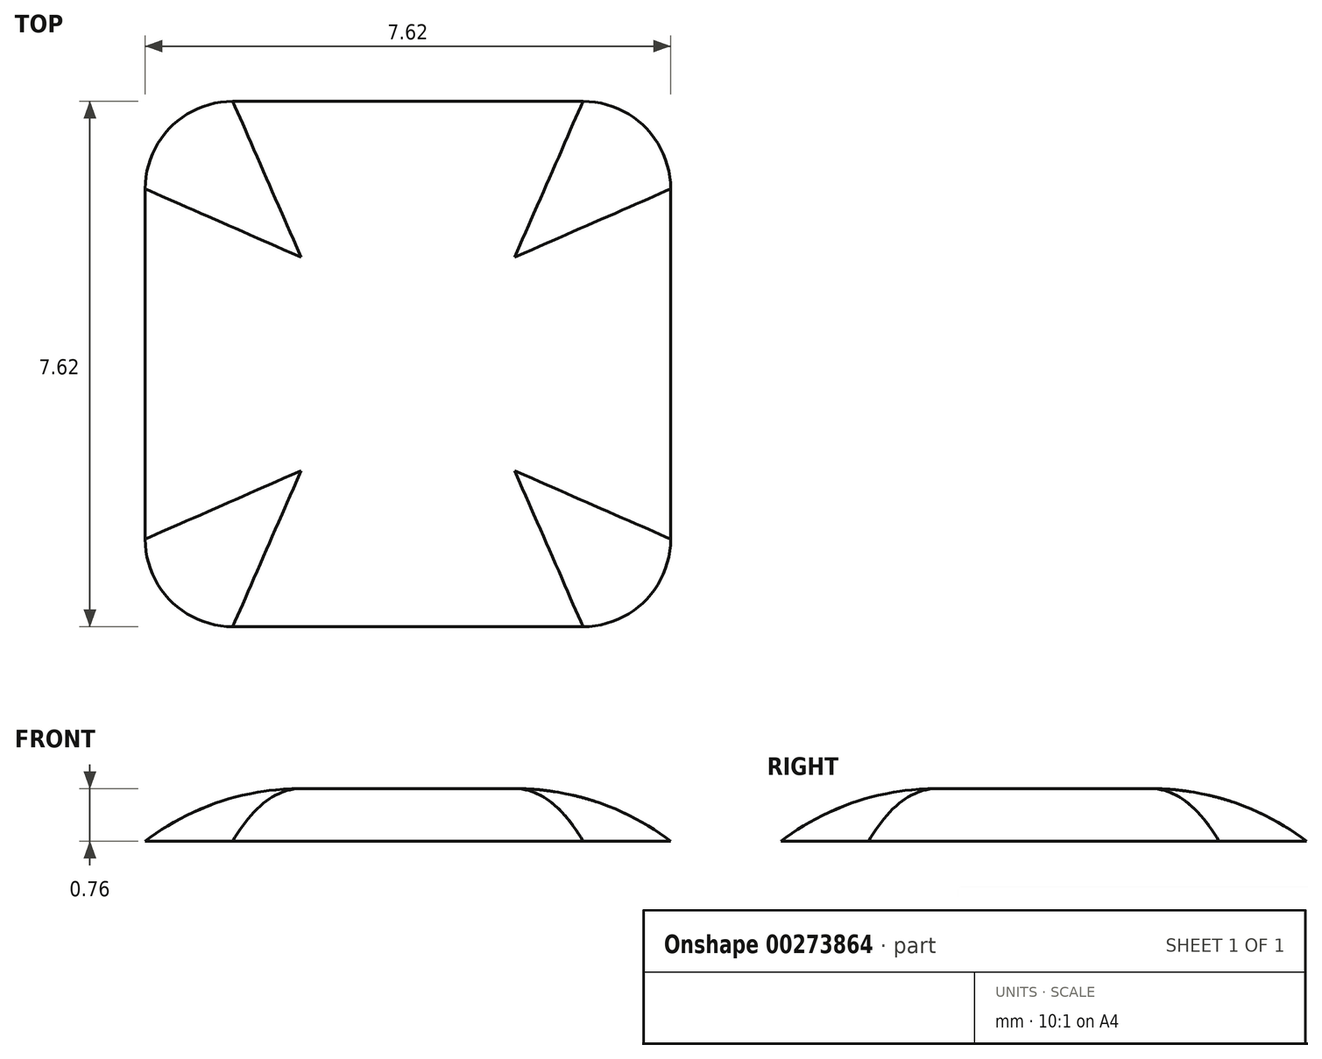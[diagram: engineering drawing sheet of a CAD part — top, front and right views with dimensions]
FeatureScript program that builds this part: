
annotation { "Feature Type Name" : "Feature", "Feature Type Description" : "" }
export const myFeature = defineFeature(function(context is Context, id is Id, definition is map)
    precondition{}
    {
        {
            var Q0;
            Q0=qCreatedBy(makeId("Top.planeOp"),FACE);
            var sketch = newSketch(context, id + "F0", { "sketchPlane" : qUnion([Q0])});
            skLineSegment(sketch, "E0.bottom", {"start": v(2.54, -3.81) * mm, "end": v(-2.54, -3.81) * mm});
            skLineSegment(sketch, "E0.top", {"start": v(2.54, 3.81) * mm, "end": v(-2.54, 3.81) * mm});
            skLineSegment(sketch, "E0.left", {"start": v(3.81, -2.54) * mm, "end": v(3.81, 2.54) * mm});
            skLineSegment(sketch, "E0.right", {"start": v(-3.81, -2.54) * mm, "end": v(-3.81, 2.54) * mm});
            skPoint(sketch, "E0.middle", {"position": v(0, 0) * mm});
            skPoint(sketch, "E1.visualSharp", {"position": v(-3.81, 3.81) * mm});
            skArc(sketch, "E1.filletArc", {"start": v(-2.54, 3.81) * mm, "mid": v(-3.44, 3.44) * mm, "end": v(-3.81, 2.54) * mm});
            skPoint(sketch, "E2.visualSharp", {"position": v(-3.81, -3.81) * mm});
            skArc(sketch, "E2.filletArc", {"start": v(-3.81, -2.54) * mm, "mid": v(-3.44, -3.44) * mm, "end": v(-2.54, -3.81) * mm});
            skPoint(sketch, "E3.visualSharp", {"position": v(3.81, -3.8) * mm});
            skArc(sketch, "E3.filletArc", {"start": v(2.54, -3.81) * mm, "mid": v(3.44, -3.44) * mm, "end": v(3.81, -2.54) * mm});
            skPoint(sketch, "E4.visualSharp", {"position": v(3.81, 3.81) * mm});
            skArc(sketch, "E4.filletArc", {"start": v(3.81, 2.54) * mm, "mid": v(3.44, 3.44) * mm, "end": v(2.54, 3.81) * mm});
            skSolve(sketch);
        }
        {
            var Q0;
            Q0=makeQuery(id+"F0.imprint","IMPRINT",FACE,{"disambiguationData":[TD([[makeQuery(id+"F0.imprint","IMPRINT",EDGE,{"derivedFrom":sQuery(id+"F0.wireOp",EDGE,"E0.bottom")}),-1.0]])]});
            extrude(context, id + "F1", {"entities" : qUnion([Q0]), "depth" : 0.76 * mm});
        }
        {
            var Q0;
            Q0=makeQuery(id+"F1.opExtrude","CAP_EDGE",EDGE,{"disambiguationData":[OSD([sQuery(id+"F0.wireOp",EDGE,"E0.left")])],"isStart":false});
            var Q1;
            Q1=makeQuery(id+"F1.opExtrude","CAP_EDGE",EDGE,{"disambiguationData":[OSD([sQuery(id+"F0.wireOp",EDGE,"E0.right")])],"isStart":false});
            fillet(context, id + "F2", {"entities" : qUnion([Q0, Q1]), "radius" : 3.74 * mm, "tangentPropagation" : true, "allowEdgeOverflow" : false});
        }
    });
